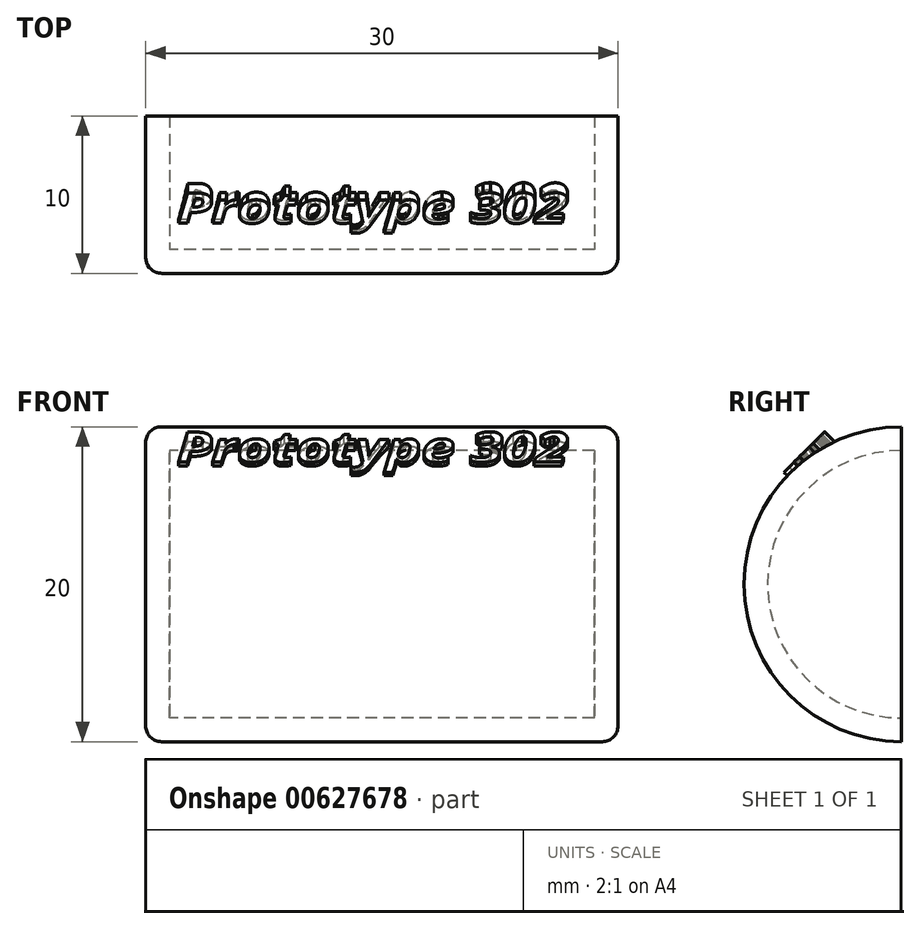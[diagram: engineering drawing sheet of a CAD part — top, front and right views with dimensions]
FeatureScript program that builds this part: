
annotation { "Feature Type Name" : "Feature", "Feature Type Description" : "" }
export const myFeature = defineFeature(function(context is Context, id is Id, definition is map)
    precondition{}
    {
        {
            var Q0;
            Q0=qCreatedBy(makeId("Front.planeOp"),FACE);
            var sketch = newSketch(context, id + "F0", { "sketchPlane" : qUnion([Q0])});
            skLineSegment(sketch, "E0", {"start": v(0, 0) * mm, "end": v(0, 10) * mm});
            skLineSegment(sketch, "E1", {"start": v(0, 10) * mm, "end": v(30, 10) * mm});
            skLineSegment(sketch, "E2", {"start": v(30, 10) * mm, "end": v(30, 0) * mm});
            skLineSegment(sketch, "E3", {"start": v(30, 0) * mm, "end": v(0, 0) * mm});
            skSolve(sketch);
        }
        {
            var Q0;
            Q0 = qSketchRegion(id + "F0", true);
            var Q1;
            Q1=sQuery(id+"F0.wireOp",EDGE,"E3");
            revolve(context, id + "F1", {"surfaceOperationType" : NewSurfaceOperationType.NEW, "entities" : qUnion([Q0]), "axis" : qUnion([Q1]), "revolveType" : RevolveType.ONE_DIRECTION, "oppositeDirection" : true, "angle" : 180 * degree});
        }
        {
            var Q0;
            Q0=makeQuery(id+"F1.opRevolve","CAP_FACE",FACE,{"disambiguationData":[OSD([sQuery(id+"F0.wireOp",EDGE,"E0"),sQuery(id+"F0.wireOp",EDGE,"E1"),sQuery(id+"F0.wireOp",EDGE,"E2"),sQuery(id+"F0.wireOp",EDGE,"E3")])],"isStart":false});
            shell(context, id + "F2", {"entities" : qUnion([Q0]), "thickness" : 1.5 * mm});
        }
        {
            var Q0;
            Q0=makeQuery(id+"F1.opRevolve","SWEPT_EDGE",EDGE,{"disambiguationData":[OSD([sQuery(id+"F0.wireOp",EDGE,"E0"),sQuery(id+"F0.wireOp",EDGE,"E1")])]});
            var Q1;
            Q1=makeQuery(id+"F1.opRevolve","SWEPT_EDGE",EDGE,{"disambiguationData":[OSD([sQuery(id+"F0.wireOp",EDGE,"E1"),sQuery(id+"F0.wireOp",EDGE,"E2")])]});
            fillet(context, id + "F3", {"entities" : qUnion([Q0, Q1]), "radius" : 1 * mm, "tangentPropagation" : true, "allowEdgeOverflow" : false});
        }
        {
            var Q0;
            Q0=qCreatedBy(makeId("Front.planeOp"),FACE);
            var Q1;
            Q1=qCreatedBy(makeId("Top.planeOp"),FACE);
            cPlane(context, id + "F4", {"entities" : qUnion([Q0, Q1]), "cplaneType" : CPlaneType.MID_PLANE, "offset" : 25 * mm, "flipAlignment" : true, "width" : 150 * mm, "height" : 150 * mm});
        }
        {
            var Q0;
            Q0=qCreatedBy(id+"F4.planeOp",FACE);
            cPlane(context, id + "F5", {"entities" : qUnion([Q0]), "cplaneType" : CPlaneType.OFFSET, "offset" : 10.3 * mm, "width" : 150 * mm, "height" : 150 * mm});
        }
        {
            var Q0;
            Q0=qCreatedBy(id+"F5.planeOp",FACE);
            var sketch = newSketch(context, id + "F6", { "sketchPlane" : qUnion([Q0])});
            skText(sketch, "E4", { "text": "Prototype 302", "fontName": "OpenSans-BoldItalic.ttf"});
            const initialGuessF6  = {"E4": [0.002, 0.00066, 1, 0, 0.00272]};
            skSetInitialGuess(sketch, initialGuessF6);
            skSolve(sketch);
        }
        {
            var Q0;
            Q0 = qSketchRegion(id + "F6", true);
            var Q1;
            Q1=makeQuery(id+"F1.opRevolve","SWEPT_FACE",FACE,{"disambiguationData":[OSD([sQuery(id+"F0.wireOp",EDGE,"E1")])]});
            extrude(context, id + "F7", {"entities" : qUnion([Q0]), "operationType" : NewBodyOperationType.ADD, "endBound" : BoundingType.UP_TO_SURFACE, "oppositeDirection" : true, "depth" : 25 * mm, "endBoundEntityFace" : qUnion([Q1]), "offsetDistance" : 25 * mm});
        }
    });
